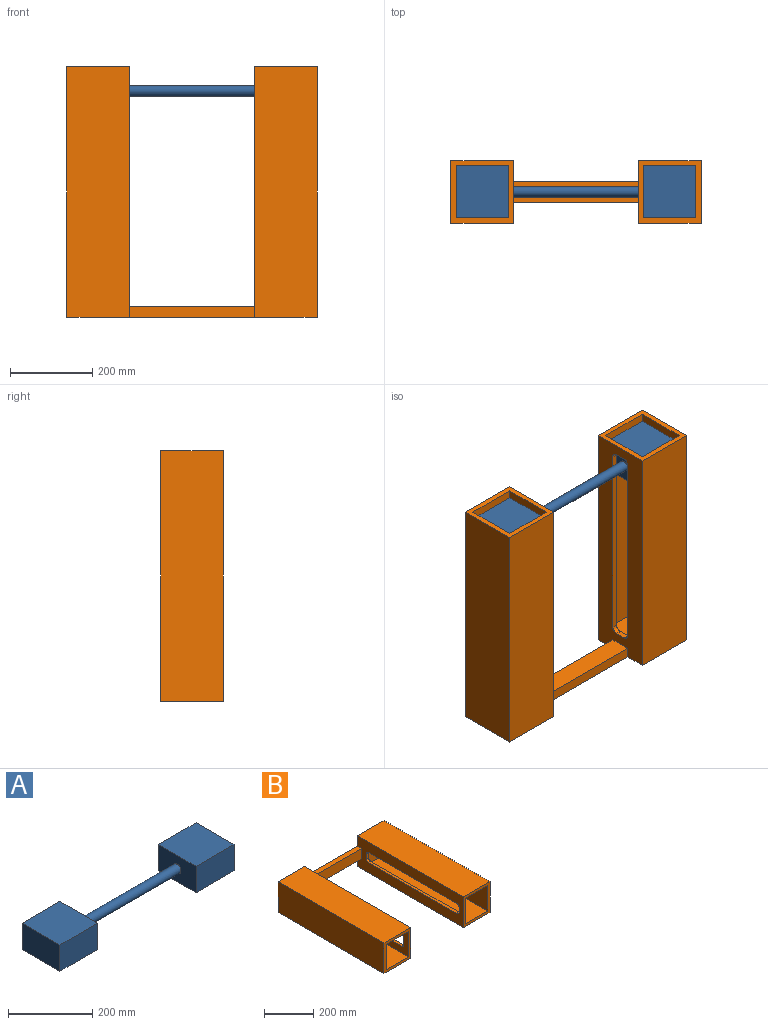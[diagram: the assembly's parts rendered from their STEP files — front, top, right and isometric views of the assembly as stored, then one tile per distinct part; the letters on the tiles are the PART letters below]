
ASSEMBLY  parts=2 mates=1
PART A: 13 faces, bbox 584.2x127x76.2 mm
  f0: plane 127x76.2mm, normal (0,1,0), area 9677.4mm2, adj f1,f3,f4,f5
  f1: plane 127x76.2mm, normal (-1,0,0), area 9677.4mm2, adj f0,f2,f4,f5
  f2: plane 127x76.2mm, normal (0,-1,0), area 9677.4mm2, adj f1,f3,f4,f5
  f3: plane 127x76.2mm, normal (1,0,0), area 9170.7mm2, adj f0,f2,f4,f5,f6
  f4: plane 127x127mm, normal (0,0,1), area 16129mm2, adj f0,f1,f2,f3
  f5: plane 127x127mm, normal (0,0,-1), area 16129mm2, adj f0,f1,f2,f3
  f6: cylinder r=12.7mm len=330.2mm, axis (-1,0,0), area 26348.8mm2, adj f3,f12
  f7: plane 127x127mm, normal (0,0,-1), area 16129mm2, adj f8,f10,f11,f12
  f8: plane 127x76.2mm, normal (0,1,0), area 9677.4mm2, adj f7,f9,f11,f12
  f9: plane 127x127mm, normal (0,0,1), area 16129mm2, adj f8,f10,f11,f12
  f10: plane 127x76.2mm, normal (0,-1,0), area 9677.4mm2, adj f7,f9,f11,f12
  f11: plane 127x76.2mm, normal (1,0,0), area 9677.4mm2, adj f7,f8,f9,f10
  f12: plane 127x76.2mm, normal (-1,0,0), area 9170.7mm2, adj f6,f7,f8,f9,f10
PART B: 40 faces, bbox 609.6x609.6x152.4 mm
  f0: plane 609.6x152.4mm, normal (1,0,0), area 61302.3mm2, adj f2,f3,f8,f9,f11,f12,f16,f24
  f1: plane 579.12x127mm, normal (-1,0,0), area 43237.8mm2, adj f14,f15,f16,f17,f24,f25,f26,f27
  f2: plane 304.8x50.8mm, normal (0,-1,0), area 15483.8mm2, adj f0,f3,f4,f8
  f3: plane 304.8x25.4mm, normal (0,0,-1), area 7741.9mm2, adj f0,f2,f4,f12
  f4: plane 609.6x152.4mm, normal (-1,0,0), area 64654.5mm2, adj f2,f3,f5,f7,f8,f12,f22,f32
  f5: plane 609.6x152.4mm, normal (0,0,-1), area 92903mm2, adj f4,f6,f12,f22
  f6: plane 609.6x152.4mm, normal (1,0,0), area 92903mm2, adj f5,f7,f12,f22
  f7: plane 609.6x152.4mm, normal (0,0,1), area 92903mm2, adj f4,f6,f12,f22
  f8: plane 304.8x25.4mm, normal (0,0,1), area 7741.9mm2, adj f0,f2,f4,f12
  f9: plane 609.6x152.4mm, normal (0,0,1), area 92903mm2, adj f0,f10,f12,f16
  f10: plane 609.6x152.4mm, normal (-1,0,0), area 92903mm2, adj f9,f11,f12,f16
  f11: plane 609.6x152.4mm, normal (0,0,-1), area 92903mm2, adj f0,f10,f12,f16
  f12: plane 609.6x152.4mm, normal (0,1,0), area 61935.4mm2, adj f0,f3,f4,f5,f6,f7,f8,f9
  f13: plane 579.12x127mm, normal (1,0,0), area 73548.2mm2, adj f14,f15,f16,f17
  f14: plane 579.12x127mm, normal (0,0,-1), area 73548.2mm2, adj f1,f13,f16,f17
  f15: plane 579.12x127mm, normal (0,0,1), area 73548.2mm2, adj f1,f13,f16,f17
  f16: plane 152.4x152.4mm, normal (0,-1,0), area 7096.8mm2, adj f0,f1,f9,f10,f11,f13,f14,f15
  f17: plane 127x127mm, normal (0,-1,0), area 16129mm2, adj f1,f13,f14,f15
  f18: plane 579.12x127mm, normal (0,0,1), area 73548.2mm2, adj f19,f21,f22,f23
  f19: plane 579.12x127mm, normal (1,0,0), area 46590mm2, adj f18,f20,f22,f23,f32,f33,f34,f35
  f20: plane 579.12x127mm, normal (0,0,-1), area 73548.2mm2, adj f19,f21,f22,f23
  f21: plane 579.12x127mm, normal (-1,0,0), area 73548.2mm2, adj f18,f20,f22,f23
  f22: plane 152.4x152.4mm, normal (0,-1,0), area 7096.8mm2, adj f4,f5,f6,f7,f18,f19,f20,f21
  f23: plane 127x127mm, normal (0,-1,0), area 16129mm2, adj f18,f19,f20,f21
  f24: plane 508x12.7mm, normal (0,0,1), area 6451.6mm2, adj f0,f1,f28,f31
  f25: plane 31.68x12.7mm, normal (0,-1,0), area 402.4mm2, adj f0,f1,f28,f29
  f26: plane 508x12.7mm, normal (0,0,-1), area 6451.6mm2, adj f0,f1,f29,f30
  f27: plane 31.68x12.7mm, normal (0,1,0), area 402.4mm2, adj f0,f1,f30,f31
  f28: cylinder r=12.7mm len=12.7mm, axis (-1,0,0), area 253.4mm2, adj f0,f1,f24,f25
  f29: cylinder r=12.7mm len=12.7mm, axis (-1,0,0), area 253.4mm2, adj f0,f1,f25,f26
  f30: cylinder r=12.7mm len=12.7mm, axis (-1,0,0), area 253.4mm2, adj f0,f1,f26,f27
  f31: cylinder r=12.7mm len=12.7mm, axis (-1,0,0), area 253.4mm2, adj f0,f1,f24,f27
  f32: plane 25.4x12.7mm, normal (0,-1,0), area 322.6mm2, adj f4,f19,f36,f39
  f33: plane 508x12.7mm, normal (0,0,1), area 6451.6mm2, adj f4,f19,f36,f37
  f34: plane 25.4x12.7mm, normal (0,1,0), area 322.6mm2, adj f4,f19,f37,f38
  f35: plane 508x12.7mm, normal (0,0,-1), area 6451.6mm2, adj f4,f19,f38,f39
  f36: cylinder r=12.7mm len=12.7mm, axis (1,0,0), area 253.4mm2, adj f4,f19,f32,f33
  f37: cylinder r=12.7mm len=12.7mm, axis (-1,0,0), area 253.4mm2, adj f4,f19,f33,f34
  f38: cylinder r=12.7mm len=12.7mm, axis (1,0,0), area 253.4mm2, adj f4,f19,f34,f35
  f39: cylinder r=12.7mm len=12.7mm, axis (-1,0,0), area 253.4mm2, adj f4,f19,f32,f35
PLACE A t=(-376.49,-80.26,336.19)mm
PLACE B rot(axis=(-1,0,0),90deg) t=(-70.26,-101.62,-176.89)mm fixed
MATE slider A.f5 <-> B.f17  axis (0,0,-1) through (-392.67,-76.22,336.19)mm
